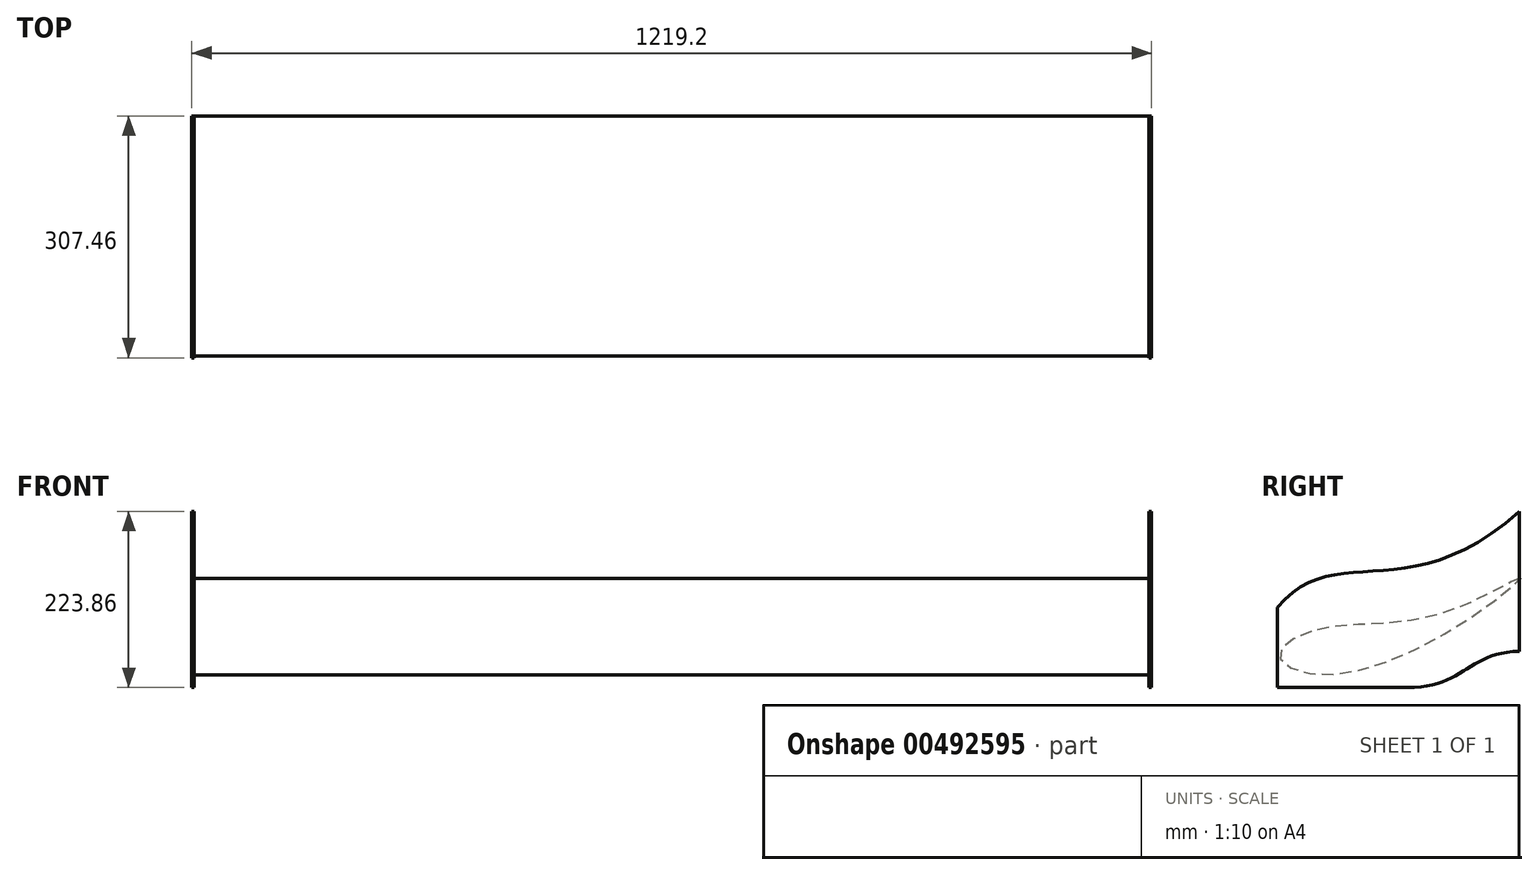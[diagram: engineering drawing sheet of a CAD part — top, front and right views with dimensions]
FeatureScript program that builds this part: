
annotation { "Feature Type Name" : "Feature", "Feature Type Description" : "" }
export const myFeature = defineFeature(function(context is Context, id is Id, definition is map)
    precondition{}
    {
        {
            var Q0;
            Q0=qCreatedBy(makeId("Right.planeOp"),FACE);
            var sketch = newSketch(context, id + "F0", { "sketchPlane" : qUnion([Q0])});
            skFitSpline(sketch, "E0", {"points": [v(0, 0) * mm, v(-102.16, -45.85) * mm, v(-255.27, -64.61) * mm, v(-304.8, -97.64) * mm, v(-250.01, -122.4) * mm, v(-66.14, -52.6) * mm, v(0, 0) * mm]});
            skSolve(sketch);
        }
        {
            var Q0;
            Q0=qCreatedBy(makeId("Right.planeOp"),FACE);
            var sketch = newSketch(context, id + "F1", { "sketchPlane" : qUnion([Q0])});
            skLineSegment(sketch, "E1", {"start": v(-307.22, -98.13) * mm, "end": v(-307.22, -138.7) * mm});
            skFitSpline(sketch, "E2", {"points": [v(-307.22, -37.1) * mm, v(0, 85.16) * mm], "startDerivative": vector(215.23, 265.33) * mm, "endDerivative": vector(423.55, 379.36) * mm});
            skLineSegment(sketch, "E3", {"start": v(-307.22, -98.13) * mm, "end": v(-307.22, -37.1) * mm});
            skLineSegment(sketch, "E4", {"start": v(0, 85.16) * mm, "end": v(0, -92.64) * mm});
            skLineSegment(sketch, "E5", {"start": v(-307.22, -138.7) * mm, "end": v(-142.12, -138.7) * mm});
            skFitSpline(sketch, "E6", {"points": [v(-142.12, -138.7) * mm, v(0, -92.64) * mm], "startDerivative": vector(212.7, -2.2) * mm, "endDerivative": vector(195.5, 2.2) * mm});
            skSolve(sketch);
        }
        {
            var Q0;
            Q0=qSketchRegion(id+"F1",true);
            extrude(context, id + "F2", {"entities" : qUnion([Q0]), "depth" : 3.17 * mm});
        }
        {
            var Q0;
            Q0=qSketchRegion(id+"F0",true);
            extrude(context, id + "F3", {"entities" : qUnion([Q0]), "operationType" : NewBodyOperationType.ADD, "depth" : 609.6 * mm});
        }
        {
            var Q0;
            Q0=makeQuery(id+"F2.opExtrude","SWEPT_BODY",BODY,{"disambiguationData":[OSD([sQuery(id+"F1.wireOp",EDGE,"E1"),sQuery(id+"F1.wireOp",EDGE,"E2"),sQuery(id+"F1.wireOp",EDGE,"E3"),sQuery(id+"F1.wireOp",EDGE,"E4"),sQuery(id+"F1.wireOp",EDGE,"E5"),sQuery(id+"F1.wireOp",EDGE,"E6")])]});
            var Q1;
            Q1=makeQuery(id+"F3.opExtrude","CAP_FACE",FACE,{"disambiguationData":[OSD([sQuery(id+"F0.wireOp",EDGE,"E0")])],"isStart":false});
            mirror(context, id + "F4", {"operationType" : NewBodyOperationType.ADD, "entities" : qUnion([Q0]), "mirrorPlane" : qUnion([Q1])});
        }
    });
